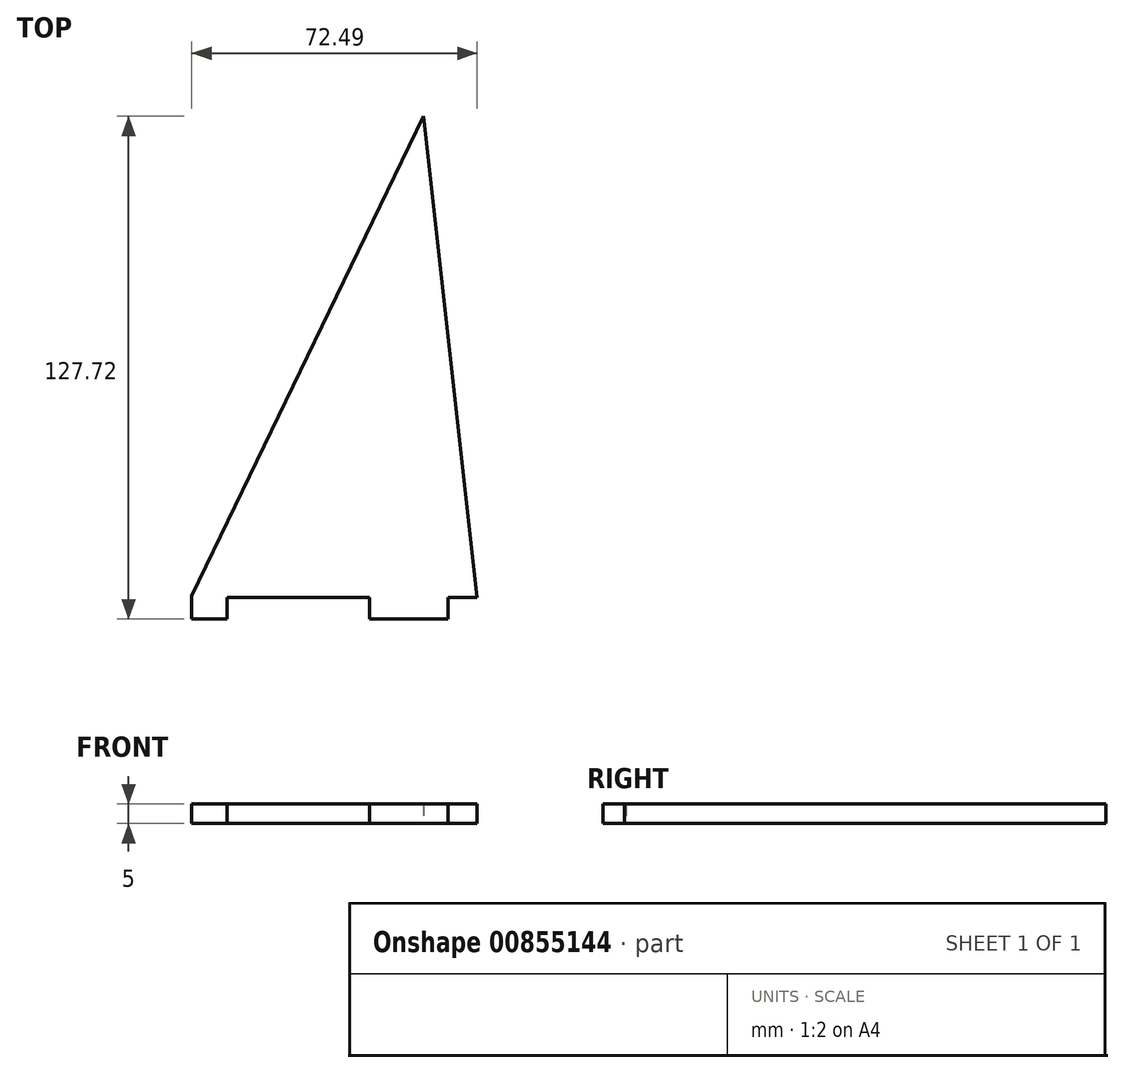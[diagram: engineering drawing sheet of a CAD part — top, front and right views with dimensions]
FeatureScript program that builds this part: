
annotation { "Feature Type Name" : "Feature", "Feature Type Description" : "" }
export const myFeature = defineFeature(function(context is Context, id is Id, definition is map)
    precondition{}
    {
        {
            var Q0;
            Q0=qCreatedBy(makeId("Top.planeOp"),FACE);
            var sketch = newSketch(context, id + "F0", { "sketchPlane" : qUnion([Q0])});
            skLineSegment(sketch, "E0", {"start": v(-45.25, -56.23) * mm, "end": v(-45.25, -62.06) * mm});
            skLineSegment(sketch, "E1", {"start": v(-45.25, -62.06) * mm, "end": v(-36.25, -62.06) * mm});
            skLineSegment(sketch, "E2", {"start": v(-36.25, -62.06) * mm, "end": v(-36.25, -56.62) * mm});
            skLineSegment(sketch, "E3", {"start": v(-36.25, -56.62) * mm, "end": v(-0.07, -56.62) * mm});
            skLineSegment(sketch, "E4", {"start": v(-0.07, -56.62) * mm, "end": v(-0.07, -62.06) * mm});
            skLineSegment(sketch, "E5", {"start": v(-0.07, -62.06) * mm, "end": v(19.93, -62.06) * mm});
            skLineSegment(sketch, "E6", {"start": v(19.93, -62.06) * mm, "end": v(19.93, -56.62) * mm});
            skLineSegment(sketch, "E7", {"start": v(19.93, -56.62) * mm, "end": v(27.24, -56.62) * mm});
            skLineSegment(sketch, "E8", {"start": v(27.24, -56.62) * mm, "end": v(13.6, 65.66) * mm});
            skLineSegment(sketch, "E9", {"start": v(13.6, 65.66) * mm, "end": v(-45.25, -56.23) * mm});
            skSolve(sketch);
        }
        {
            var Q0;
            Q0 = qSketchRegion(id + "F0", true);
            extrude(context, id + "F1", {"entities" : qUnion([Q0]), "depth" : 5 * mm, "offsetDistance" : 25 * mm});
        }
    });
